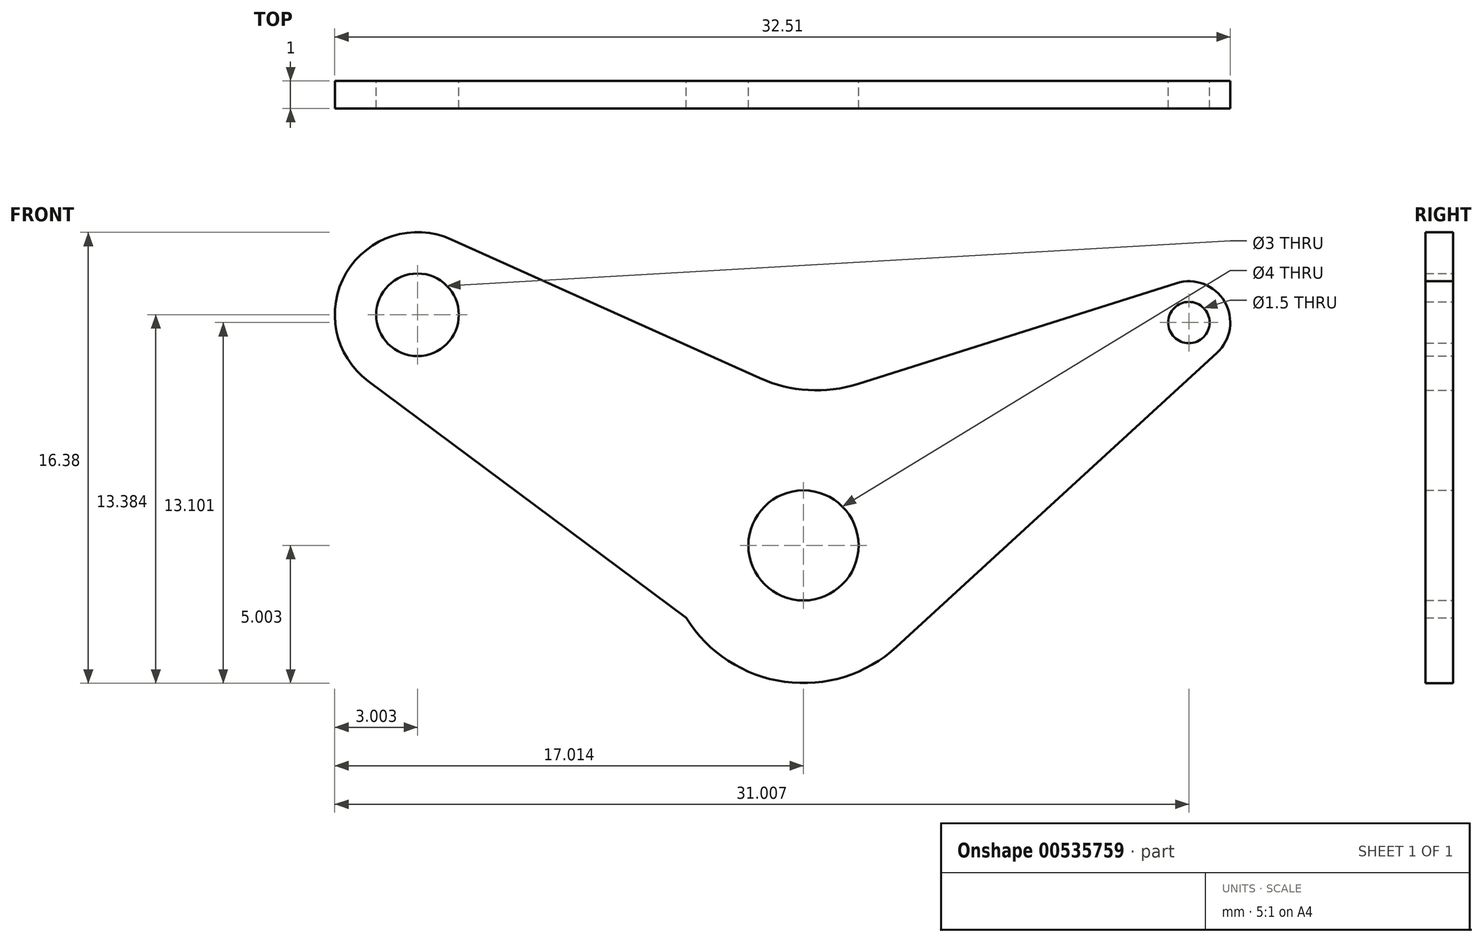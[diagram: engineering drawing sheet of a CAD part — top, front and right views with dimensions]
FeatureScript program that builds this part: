
annotation { "Feature Type Name" : "Feature", "Feature Type Description" : "" }
export const myFeature = defineFeature(function(context is Context, id is Id, definition is map)
    precondition{}
    {
        {
            var Q0;
            Q0=qCreatedBy(makeId("Front.planeOp"),FACE);
            var sketch = newSketch(context, id + "F0", { "sketchPlane" : qUnion([Q0])});
            skCircle(sketch, "E0", {"center": v(-37.19, 17.15) * mm, "radius": 1.5 * mm});
            skCircle(sketch, "E1", {"center": v(-23.18, 8.77) * mm, "radius": 2 * mm});
            skCircle(sketch, "E2", {"center": v(-9.18, 16.87) * mm, "radius": 0.75 * mm});
            skArc(sketch, "E3", {"start": v(-35.96, 19.89) * mm, "mid": v(-39.77, 18.67) * mm, "end": v(-38.98, 14.75) * mm});
            skArc(sketch, "E4", {"start": v(-27.43, 6.14) * mm, "mid": v(-23.86, 3.82) * mm, "end": v(-19.8, 5.1) * mm});
            skArc(sketch, "E5", {"start": v(-8.17, 15.77) * mm, "mid": v(-7.88, 17.62) * mm, "end": v(-9.64, 18.3) * mm});
            skLineSegment(sketch, "E6", {"start": v(-38.98, 14.75) * mm, "end": v(-27.43, 6.14) * mm});
            skLineSegment(sketch, "E7", {"start": v(-19.8, 5.1) * mm, "end": v(-8.17, 15.77) * mm});
            skLineSegment(sketch, "E8", {"start": v(-9.64, 18.3) * mm, "end": v(-21.2, 14.64) * mm});
            skLineSegment(sketch, "E9", {"start": v(-24.76, 14.85) * mm, "end": v(-35.96, 19.89) * mm});
            skPoint(sketch, "E10.visualSharp", {"position": v(-23.02, 14.07) * mm});
            skArc(sketch, "E10.filletArc", {"start": v(-24.76, 14.85) * mm, "mid": v(-23, 14.42) * mm, "end": v(-21.2, 14.64) * mm});
            skSolve(sketch);
        }
        {
            var Q0;
            Q0 = qSketchRegion(id + "F0", true);
            extrude(context, id + "F1", {"entities" : qUnion([Q0]), "endBound" : BoundingType.SYMMETRIC, "depth" : 1 * mm, "offsetDistance" : 25 * mm});
        }
    });
